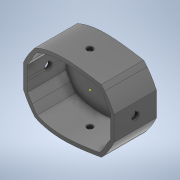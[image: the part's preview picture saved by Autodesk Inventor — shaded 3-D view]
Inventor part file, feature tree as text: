
AUTODESK INVENTOR PART (.ipt)
format: ipt  version: 2021.1 (Build 251245010, 245A)  size: 232,960 bytes
history: native  units: mm
features: extrude x4, sketch x3, plane x3, mirror x1
ambient origin geometry x8: Origin, YZ Plane, XZ Plane, XY Plane, X Axis, Y Axis, Z Axis, Center Point
bodies: Solid1 (feature_tree)
feature tree (11):
  sketch  "Sketch1"  dims[d1=70.0mm d2=70.0mm]
  sketch  "Sketch2"  dims[d3=0.0mm d4=6.0mm]
  extrude  "Extrusion1"  Depth=70.0mm
  extrude  "Extrusion2"  Depth=6.0mm
  plane  "Work Plane1"
  extrude  "Extrusion3"  TaperAngle=0.0deg  [1 undecoded]
  plane  "Work Plane2"
  sketch  "Sketch5"  dims[d5=64.0mm d6=0.0mm d7=60.0mm d9=300.0mm d10=0.0mm d11=49.151954mm d12=49.152mm d13=10.0mm d14=10.0mm d15=20.0mm d16=0.0mm d19=40.0mm d20=6.0mm d21=6.0mm]
  mirror  "Mirror1"
  plane  "Work Plane3"
  extrude  "Extrusion4"  Depth=60.0mm
note: 1 required parameter value undecoded (feature->parameter linkage not recoverable at this tier; creation-order binding heuristic only, values carry confidence <= 0.55)
